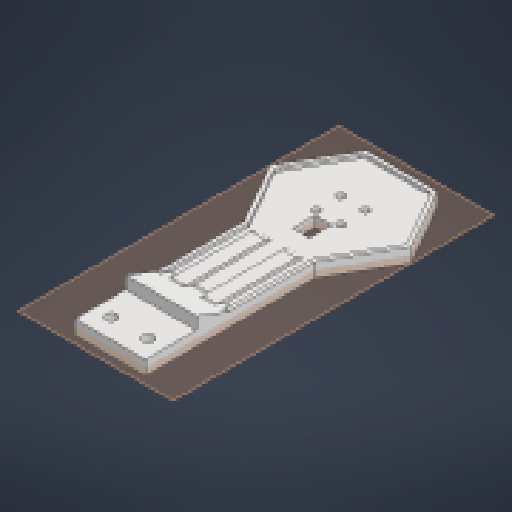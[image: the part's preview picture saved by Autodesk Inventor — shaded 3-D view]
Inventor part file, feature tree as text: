
AUTODESK INVENTOR PART (.ipt)
format: ipt  version: 2023 (Build 270158000, 158)  size: 337,408 bytes
history: native  units: in
note: dims shown in document units (in); Inventor stores cm internally (conversion verified against a paired STEP export)
features: extrude x7, sketch x6, fillet x3, projected_geometry x2, plane x1
ambient origin geometry x8: Origin, YZ Plane, XZ Plane, XY Plane, X Axis, Y Axis, Z Axis, Center Point
bodies: Solid1 (feature_tree)
feature tree (19):
  extrude  "Extrusion1"  Depth=3.0in
  extrude  "Extrusion4"  Depth=0.25in
  extrude  "Extrusion7"  Depth=0.3in
  extrude  "Extrusion8"  Depth=0.3in
  fillet  "Fillet2"  Radius=1.4375in
  fillet  "Fillet4"  Radius=1.25in
  plane  "Work Plane1"
  extrude  "Extrusion9"  Depth=0.4331in
  extrude  "Extrusion11"  Depth=0.125in
  extrude  "Extrusion12"  Depth=0.125in
  fillet  "Fillet9"  Radius=0.142in
  sketch  "Sketch4"  dims[d0=1.25in d1=3.0in]
  sketch  "Sketch8"  dims[d2=0.25in d3=0.0in d11=0.21in]
  projected_geometry  "Projected Loop2"
  sketch  "Sketch9"  dims[d12=0.35in d13=0.3in]
  projected_geometry  "Projected Loop3"
  sketch  "Sketch11"  dims[d14=0.21in d15=0.35in d16=0.3in d17=1.4375in d18=0.0in d65=1.25in]
  sketch  "Sketch13"  dims[d66=0.4331in d67=0.4331in]
  sketch  "Sketch14"  dims[d68=0.2165in d69=0.2165in d70=0.142in d71=0.142in d72=0.142in d73=0.142in d77=0.0625in d78=0.0in d79=0.2785in d80=0.125in d82=0.125in d83=1.9375in d84=0.0in d85=0.125in d87=0.125in d88=0.125in d89=0.0in d94=0.4in d96=-0.0666in d97=0.3in d98=0.15in d99=0.4in d100=0.125in d101=0.0in d102=1.25in d103=0.0in d107=0.22in d110=0.125in]
